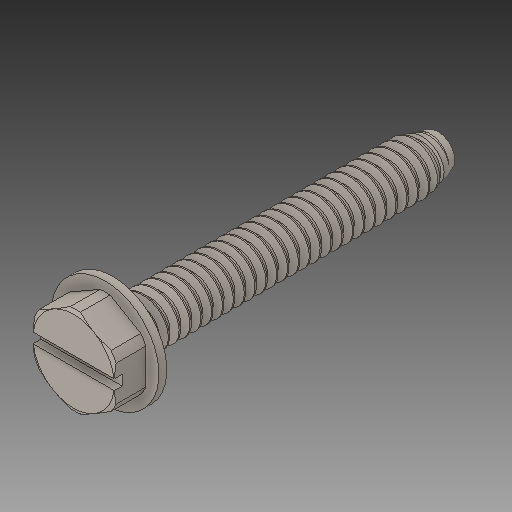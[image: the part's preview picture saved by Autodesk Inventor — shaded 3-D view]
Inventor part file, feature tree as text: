
AUTODESK INVENTOR PART (.ipt)
format: ipt  version: 2018 (Build 220112000, 112)  size: 797,696 bytes
history: native  units: in
note: dims shown in document units (in); Inventor stores cm internally (conversion verified against a paired STEP export)
features: extrude x1
ambient origin geometry x8: Origin, YZ Plane, XZ Plane, XY Plane, X Axis, Y Axis, Z Axis, Center Point
bodies: Solid1 (feature_tree)
feature tree (1):
  extrude  "Extrude4"  [1 undecoded]
note: 1 required parameter value undecoded (feature->parameter linkage not recoverable at this tier; creation-order binding heuristic only, values carry confidence <= 0.55)
